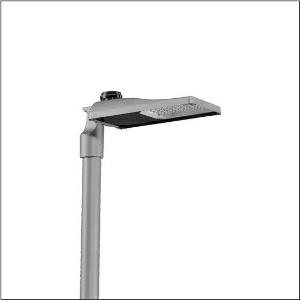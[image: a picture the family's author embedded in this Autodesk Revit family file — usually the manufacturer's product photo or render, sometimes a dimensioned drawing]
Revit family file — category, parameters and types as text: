
# Revit family: streetlight_sl_31_mini___st0_8a_5xh6c45n08ja_4560
name_source: partatom
category: Lighting Fixtures
units: mm (PartAtom-declared; Revit-internal decimal feet)

## family parameters
Cut with Voids When Loaded = No
Host = Face
Light Source = No
Part Type = Normal
Room Calculation Point = No
Round Connector Dimension = Use Diameter
Shared = No

## types (1)
- --- (1 x LED, 12590 lm, 81.1 W, 4000K)
    Apparent Load = 81 VA
    CIE Flux Codes = 41 75 97 100 100
    Color Rendering = 70
    Color Temperature = 4000K
    Default Elevation = 1800 mm
    Description = Streetlight SL 31 mini NEMA (7pin), Desk-Remote mast luminaire for post-top, side-entry; light control with lens of PMMA; light distribution: ST0.8a, direct asymmetric distribution, for standard-compliant lighting for roads and squares; LED: luminous flux: 12.590lm, light colour: 740, colour temperature: 4000K; luminous efficacy: 155,2lm/W; control: pre-setting: linear dimming characteristic, flexible luminous flux parameterisation, time-dependent luminous flux control, constant luminous flux control, intelligent temperature release in ECG and LED module, overheat protection; luminaire housing, of diecast aluminium, Siteco® metallic grey (DB 702S), corrosivity category C5 high according to DIN EN ISO 12944; cover of toughened safety glass, transparent, opened without tools; mast flange of diecast aluminium, Siteco® metallic grey (DB 702S), spigot size: 76/60mm, mast flange included unmounted; with cable H07RN-F 3x 1.5mm², cable length: 10,5m, connection cable pre-assembled; mains connection: 220..240V, AC, 50/60Hz; power consumption (at start of service life): 81,1W / (at end of service life): 88,3W / (with reduced operation 50%): 36,4W; protection rating (complete): IP66; insulation class (complete): insulation class I (protective earthing); impact resistance: IK10; certification: CE, ENEC, ENEC+, VDE, UKCA; permissible operating ambient temperature for outdoor applications: -40..+50°C; packaging unit: 1 piece

Light Distribution: ST0.8a
    Height = 76 mm
    Lamp = 1 x LED
    Lamp Light Flux = 12590 lm
    Lamp Power = 81.1 W
    Lamp count = 1
    Length = 547 mm
    Luminous efficacy = 155 lm/W
    Manufacturer = Siteco
    ModVariant = No
    Model = 5XH6C45N08JA
    Number of Poles = 1
    OnlyDefault = Yes
    Power Factor = 1
    Product Name = Streetlight SL 31 mini | ST0.8a
    Product group = mast luminaire | pylon top
    ProductGroupID = 6100
    Protection Class = Protection class I
    Protection Degree = IP 66
    RLX_Detail_Level = 1
    RLX_Emergency_Light_Flux = 0 lm
    RLX_Emergency_Type = 0
    RLX_Emergency_Type_DB = No
    RlxData = <blob elided: 40369 chars, md5=cb911144>
    Socket = socket
    Standby Power = 0 W
    System Light Flux = 12590 lm
    System Power = 81 W
    Type Comments = factory setting: luminous flux: 100 % | dim-lin: 254 | 860 mA
    Type Image = l_1300322.jpg
    URL = http://relux.com
    VarID = @adj_070091
    Voltage = 0 V
    Weight = 0.00 kg
    Width = 265 mm

## geometry (parser evidence)
native form markers: Blend x4, Sweep x11
no freeform markers — native parametric forms only
